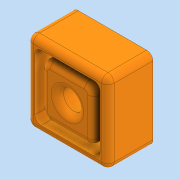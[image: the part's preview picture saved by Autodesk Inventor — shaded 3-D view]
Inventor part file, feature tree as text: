
AUTODESK INVENTOR PART (.ipt)
format: ipt  version: 2020 (Build 240168000, 168)  size: 241,152 bytes
history: native  units: mm
features: extrude x5, sketch x5, fillet x3
ambient origin geometry x8: Origin, YZ Plane, XZ Plane, XY Plane, X Axis, Y Axis, Z Axis, Center Point
bodies: Solido1 (feature_tree)
feature tree (13):
  extrude  "Estrusione1"  Depth=17.0mm
  extrude  "Estrusione2"  Depth=10.0mm TaperAngle=0.0deg
  extrude  "Estrusione6"  Depth=26.0mm
  fillet  "Raccordo3"  Radius=26.0mm
  fillet  "Raccordo8"  Radius=4.5mm
  extrude  "Estrusione9"  Depth=2.0mm
  fillet  "Raccordo9"  Radius=3.0mm
  extrude  "Estrusione10"  Depth=21.0mm
  sketch  "Schizzo1"
  sketch  "Schizzo2"
  sketch  "Schizzo12"
  sketch  "Schizzo20"
  sketch  "Schizzo21"
